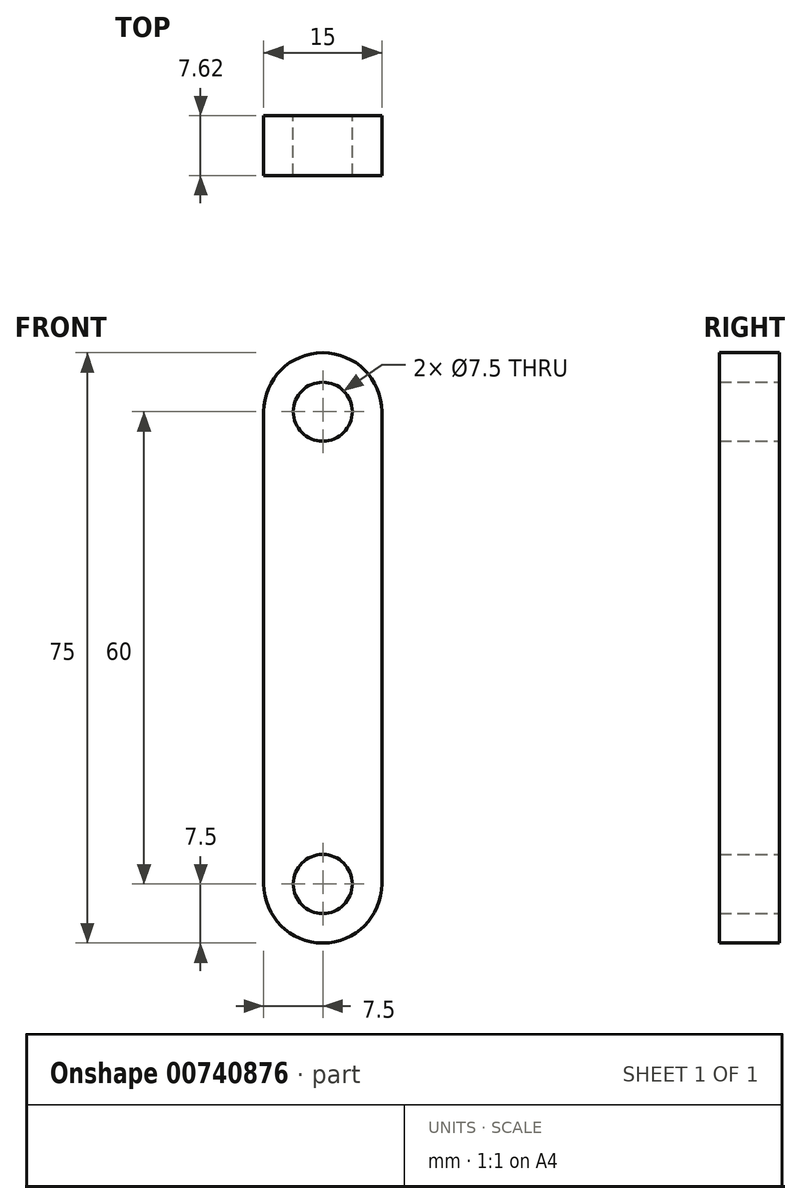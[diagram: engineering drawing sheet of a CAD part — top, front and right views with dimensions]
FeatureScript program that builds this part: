
annotation { "Feature Type Name" : "Feature", "Feature Type Description" : "" }
export const myFeature = defineFeature(function(context is Context, id is Id, definition is map)
    precondition{}
    {
        {
            var Q0;
            Q0=qCreatedBy(makeId("Front.planeOp"),FACE);
            var sketch = newSketch(context, id + "F0", { "sketchPlane" : qUnion([Q0])});
            skCircle(sketch, "E0", {"center": v(0, 0) * mm, "radius": 3.75 * mm});
            skCircle(sketch, "E1", {"center": v(0, 60) * mm, "radius": 3.75 * mm});
            skCircle(sketch, "E2", {"center": v(0, 60) * mm, "radius": 7.5 * mm});
            skCircle(sketch, "E3", {"center": v(0, 0) * mm, "radius": 7.5 * mm});
            skLineSegment(sketch, "E4", {"start": v(-7.5, 0) * mm, "end": v(-7.5, 60) * mm});
            skLineSegment(sketch, "E5", {"start": v(7.5, 60) * mm, "end": v(7.5, 0) * mm});
            skSolve(sketch);
        }
        {
            var Q0;
            {var subQ0=sQuery(id+"F0.wireOp",EDGE,"E4");Q0=makeQuery(id+"F0.imprint","IMPRINT",FACE,{"disambiguationData":[TD([[makeQuery(id+"F0.imprint","IMPRINT",EDGE,{"derivedFrom":subQ0}),-1.0]])]});}
            var Q1;
            Q1=makeQuery(id+"F0.imprint","IMPRINT",FACE,{"disambiguationData":[TD([[makeQuery(id+"F0.imprint","IMPRINT",EDGE,{"derivedFrom":sQuery(id+"F0.wireOp",EDGE,"E1")}),-1.0]])]});
            var Q2;
            Q2=makeQuery(id+"F0.imprint","IMPRINT",FACE,{"disambiguationData":[TD([[makeQuery(id+"F0.imprint","IMPRINT",EDGE,{"derivedFrom":sQuery(id+"F0.wireOp",EDGE,"E0")}),-1.0]])]});
            extrude(context, id + "F1", {"entities" : qUnion([Q0, Q1, Q2]), "depth" : 7.62 * mm, "offsetDistance" : 25.4 * mm});
        }
    });
